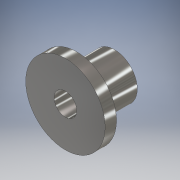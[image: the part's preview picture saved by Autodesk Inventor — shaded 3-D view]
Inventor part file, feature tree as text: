
AUTODESK INVENTOR PART (.ipt)
format: ipt  version: 2017 (Build 210142000, 142)  size: 122,880 bytes
history: native  units: mm
features: extrude x3, sketch x3, chamfer x1
ambient origin geometry x8: Origin, YZ Plane, XZ Plane, XY Plane, X Axis, Y Axis, Z Axis, Center Point
bodies: Solid1 (feature_tree)
feature tree (7):
  extrude  "Extrusion1"  Depth=3.0mm TaperAngle=0.0deg
  extrude  "Extrusion3"  Depth=10.0mm TaperAngle=0.0deg
  extrude  "Extrusion5"  Depth=3.0mm TaperAngle=0.0deg
  chamfer  "Chamfer1"  Distance=3.0mm Angle=45.0deg
  sketch  "Sketch1"  dims[d0=21.0mm d1=3.0mm d2=0.0mm]
  sketch  "Sketch2"  dims[d3=12.0mm d8=10.0mm d9=0.0mm]
  sketch  "Sketch4"  dims[d13=6.0mm d14=12.9mm d15=0.0mm d16=3.0mm d17=2.0mm d18=45.0deg]
